# Revit family: Molior 4 Corner - Ceiling based
name_source: partatom
category: Lighting Fixtures
revit_build: Autodesk Revit Architecture 2014 (Build: 20130308_1515(x64)
units: mm (PartAtom-declared; Revit-internal decimal feet)

## types (5) — shared parameters
ArticleNumber = See URL hyperlink
AssetType = Moveable/Fixed
BSAB 96 = SNB.2
BallastsCELMAEnergyEfficiencyIndex = Class A1/A2
CCSClassCode = UAC
CCSClassName = Belysningsarmatur
CCSTopnode = L
Cassette Depth = 0.00 mm
Cassette Width = 0.00 mm
Clearance Zones = Yes
Clearance Zones Offset = 60.00 mm
Color Filter = 16777215
Colour = White
ControlGearPosition = Integrated
Description = 70-80-35 General Lighting Systems
Dimming Lamp Color Temperature Shift = <None>
DocumentReference = See URL hyperlink
Documentation = See URL hyperlink
Finish = Powder coated
Frame = Riegens_Steel_Powder coated white RAL901025
Frame Offset = 0.00 mm
Frame Thickness = 35.00 mm
Glass = Riegens_Glass_opal
HasProtectiveEarth = TRUE
IP_Code = IP20
IfcExportAs = IfcLightFixtureType
IfcExportType = NOTDEFINED
InsulationStandardClass = Class 1
InternalFuse = Only required in emergency versions
LampColourRenderingIndex = Ra>80 / Ra>90 on request
LampRating = 25W / 31W
LampType = LED
LightFixtureMountingType = Recessed
LightFixturePlacingType = Ceiling
LightSource = LED 3000K / 4000K
LuminairePowerFactor = >0,9
LuminaireType = Recessed Direct LED Luminaire
Manufacturer = Riegens A/S
ManufacturerURL = www.riegens.com
Material = Steel and optic from PMMA.
NominalVoltage = 220-240V
Optic = Direct Collimating TIR optic
PhaseReference = IEC recommendations
Photometric Web File = Molior 4 corner 31W 4000K Lens Clear.ies
PhotometricPerformance = In accordance with BS EN 13032-1
ProductInformation = http://riegens.com
Shape = Square
Tilt Angle = 90.00°
Total height with brackets = 100.00 mm
TotalWattage = Max. 27W / 33W
Uniclass 1.4 = JY73
Uniclass2 = Pr_70_70_49_43 Light-Emitting Diode (LED) Luminaires

## per-type parameters (varying)
| type | BIMObjectName | Bracket for C ceilings | Frame Length | Frame Width | Size |
| Molior 4 Corner 625x625 C | Molior 4 Corner 625x625 C.rfa | Yes | 624.00 mm | 624.00 mm | 624 x 624 x 100 mm |
| Molior 4 Corner 600x600 C | Molior 4 Corner 600x600 C.rfa | Yes | 599.00 mm | 599.00 mm | 599 x 599 x 100 mm |
| Molior 4 Corner 600x600 SAS 130 | Molior 4 Corner 600x600 SAS 130.rfa | No | 584.00 mm | 584.00 mm | 584 x 584 x 35 mm |
| Molior 4 Corner 600x600 TL | Molior 4 Corner 600x600 TL.rfa | No | 595.00 mm | 595.00 mm | 595 x 595 x 35 mm |
| Molior 4 Corner 625x625 TL | Molior 4 Corner 625x625 TL.rfa | No | 620.00 mm | 620.00 mm | 620 x 620 x 35 mm |

note: column(s) folded — value = type name in every type: ModelReference

## geometry (parser evidence)
native form markers: Blend x78, Sweep x4
no freeform markers — native parametric forms only
